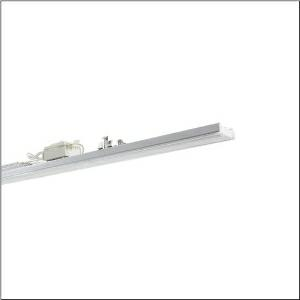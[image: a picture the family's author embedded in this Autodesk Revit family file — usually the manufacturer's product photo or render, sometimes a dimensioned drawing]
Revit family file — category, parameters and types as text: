
# Revit family: licross_r__21_recessed_mo_51te18vn465g_3c09
name_source: partatom
category: Lighting Fixtures
units: mm (PartAtom-declared; Revit-internal decimal feet)

## family parameters
Cut with Voids When Loaded = No
Host = Face
Light Source = No
Part Type = Normal
Room Calculation Point = No
Round Connector Dimension = Use Diameter
Shared = No

## types (1)
- --- (1 x LED, 6500 lm, 35.3 W, 4000K)
    Apparent Load = 35 VA
    CIE Flux Codes = 83 96 99 100 100
    Color Rendering = 80
    Color Temperature = 4000K
    Default Elevation = 1800 mm
    Description = Licross® 21 Recessed MO, luminaire insert, of sheet steel, galvanised, coil coated, white, length: 1.500mm, width: 66mm, height: 67mm, LED rated luminous flux: 6.500lm, light colour: 840, control gear: DALI 2, CLO, with plug, 5-pole, with phase selection, mains connection: 220..240V, AC, 50/60Hz, start of lifetime: 35W, end of service life: 39W, internal wiring halogen-free, primary light control with lens, of plastic, primary optical cover: cover, of PMMA, light emission: direct distribution, primary light characteristic: symmetric, protection rating (complete): IP54, insulation class (complete): insulation class I (protective earthing), certification: CE, ENEC, VDE, UKCA, protection symbol: D if used in an environment with non-conductive dust loads with corresponding accessories, impact resistance: IK06, permissible ambient temperature for indoor applications: -25..+40°C, corresponds to IFS (International Featured Standards) requirements for safety and quality in the food industry, reducing of maximum allowable ambient temperature of 5°C with ceiling mounting, LABS conformity tested according to VDMA 24364:2018-05, packaging unit: 1 piece
    Height = 58 mm
    Lamp = 1 x LED
    Lamp Light Flux = 6500 lm
    Lamp Power = 35.3 W
    Lamp count = 1
    Length = 1500 mm
    Luminous efficacy = 184 lm/W
    Manufacturer = Siteco
    ModVariant = No
    Model = 51TE18VN465G
    Mounting Place = Ceiling
    Mounting Type = Pendant
    Number of Poles = 1
    OnlyDefault = Yes
    Power Factor = 1
    Product Name = Licross® 21 Recessed MO
    Product group = luminaire insert | ceiling pendant
    ProductGroupID = 902
    Protection Class = Protection class I
    Protection Degree = IP 54
    RLX_Detail_Level = 1
    RLX_Emergency_Light_Flux = 0 lm
    RLX_Emergency_Type = 0
    RLX_Emergency_Type_DB = No
    RlxData = <blob elided: 24369 chars, md5=de1d6bce>
    Socket = socket
    Standby Power = 0 W
    System Light Flux = 6500 lm
    System Power = 35 W
    Type Comments = factory setting: luminous flux: 100 % | dim-lin: 254 | 239 mA
    Type Image = l_1296930.jpg
    URL = http://relux.com
    VarID = @adj_108571
    Voltage = 0 V
    Weight = 0.00 kg
    Width = 66 mm

## geometry (parser evidence)
native form markers: Blend x4, Sweep x11
no freeform markers — native parametric forms only
